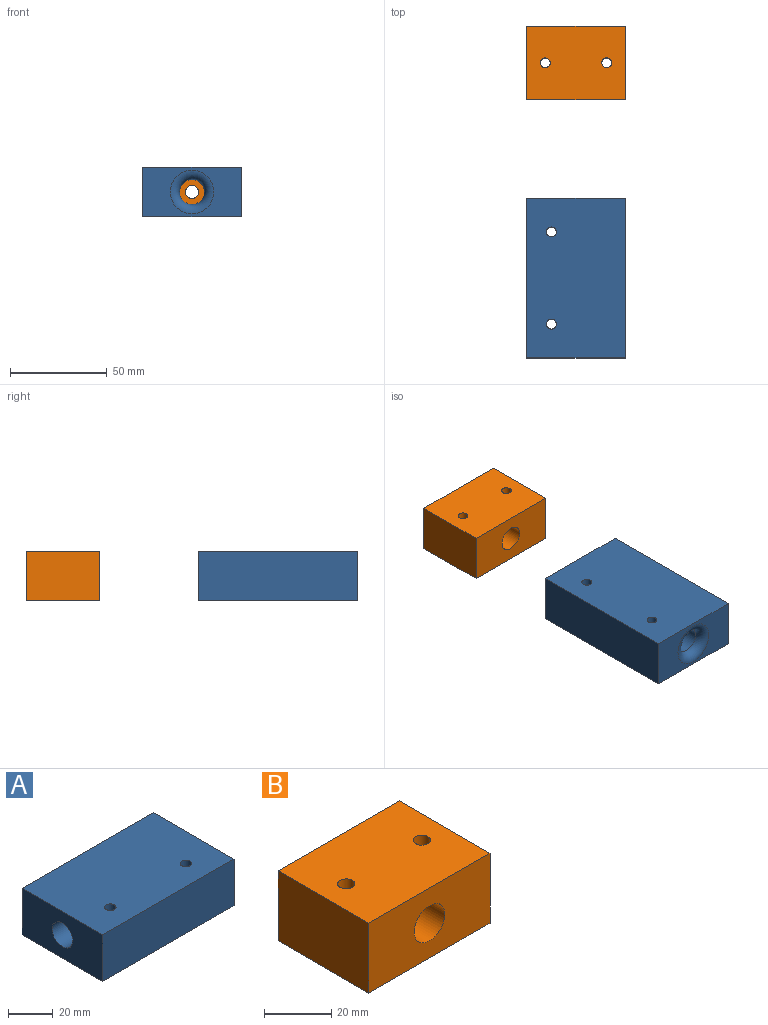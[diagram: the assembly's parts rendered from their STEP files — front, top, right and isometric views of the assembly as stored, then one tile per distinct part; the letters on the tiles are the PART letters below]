
ASSEMBLY  parts=2 mates=1
PART A: 10 faces, bbox 82.6x50.8x25.4 mm
  f0: plane 82.55x25.4mm, normal (0,1,0), area 2096.8mm2, adj f1,f3,f4,f5
  f1: plane 50.8x25.4mm, normal (-1,0,0), area 1161.1mm2, adj f0,f2,f4,f5,f8
  f2: plane 82.55x25.4mm, normal (0,-1,0), area 2096.8mm2, adj f1,f3,f4,f5
  f3: plane 50.8x25.4mm, normal (1,0,0), area 893.5mm2, adj f0,f2,f4,f5,f9
  f4: plane 82.55x50.8mm, normal (0,0,1), area 4152.6mm2, adj f0,f1,f2,f3,f6,f7
  f5: plane 82.55x50.8mm, normal (0,0,-1), area 4152.6mm2, adj f0,f1,f2,f3,f6,f7
  f6: cylinder r=2.55mm len=25.4mm, axis (0,0,1), area 407.4mm2, adj f4,f5
  f7: cylinder r=2.55mm len=25.4mm, axis (0,0,1), area 407.4mm2, adj f4,f5
  f8: cylinder r=6.41mm len=77.72mm, axis (1,0,0), area 3132.1mm2, adj f1,f9
  f9: torus R=11.24mm, axis (1,0,0), area 389mm2, adj f3,f8
PART B: 13 faces, bbox 50.8x38.1x25.4 mm
  f0: cylinder r=3.38mm len=18.29mm, axis (0,1,0), area 388.2mm2, adj f9,f11
  f1: plane 50.8x25.4mm, normal (0,1,0), area 1193.3mm2, adj f2,f4,f5,f6,f10
  f2: plane 38.1x25.4mm, normal (-1,0,0), area 967.7mm2, adj f1,f3,f5,f6
  f3: plane 50.8x25.4mm, normal (0,-1,0), area 1161.1mm2, adj f2,f4,f5,f6,f12
  f4: plane 38.1x25.4mm, normal (1,0,0), area 967.7mm2, adj f1,f3,f5,f6
  f5: plane 50.8x38.1mm, normal (0,0,1), area 1894.5mm2, adj f1,f2,f3,f4,f7,f8
  f6: plane 50.8x38.1mm, normal (0,0,-1), area 1894.5mm2, adj f1,f2,f3,f4,f7,f8
  f7: cylinder r=2.55mm len=25.4mm, axis (0,0,1), area 407.4mm2, adj f5,f6
  f8: cylinder r=2.55mm len=25.4mm, axis (0,0,1), area 407.4mm2, adj f5,f6
  f9: plane 11.11x11.11mm, normal (0,1,0), area 61.1mm2, adj f0,f10
  f10: cylinder r=5.56mm len=11.11mm, axis (0,1,0), area 248.3mm2, adj f1,f9
  f11: plane 12.83x12.83mm, normal (0,-1,0), area 93.4mm2, adj f0,f12
  f12: cylinder r=6.41mm len=12.83mm, axis (0,-1,0), area 511.8mm2, adj f3,f11
PLACE A rot(axis=(0,0,-1),90deg) t=(50.8,-88.9,0)mm
PLACE B at identity fixed
MATE fastened B.f0 <-> A.f8  axis (0,-1,0) through (25.4,-38.1,12.7)mm
